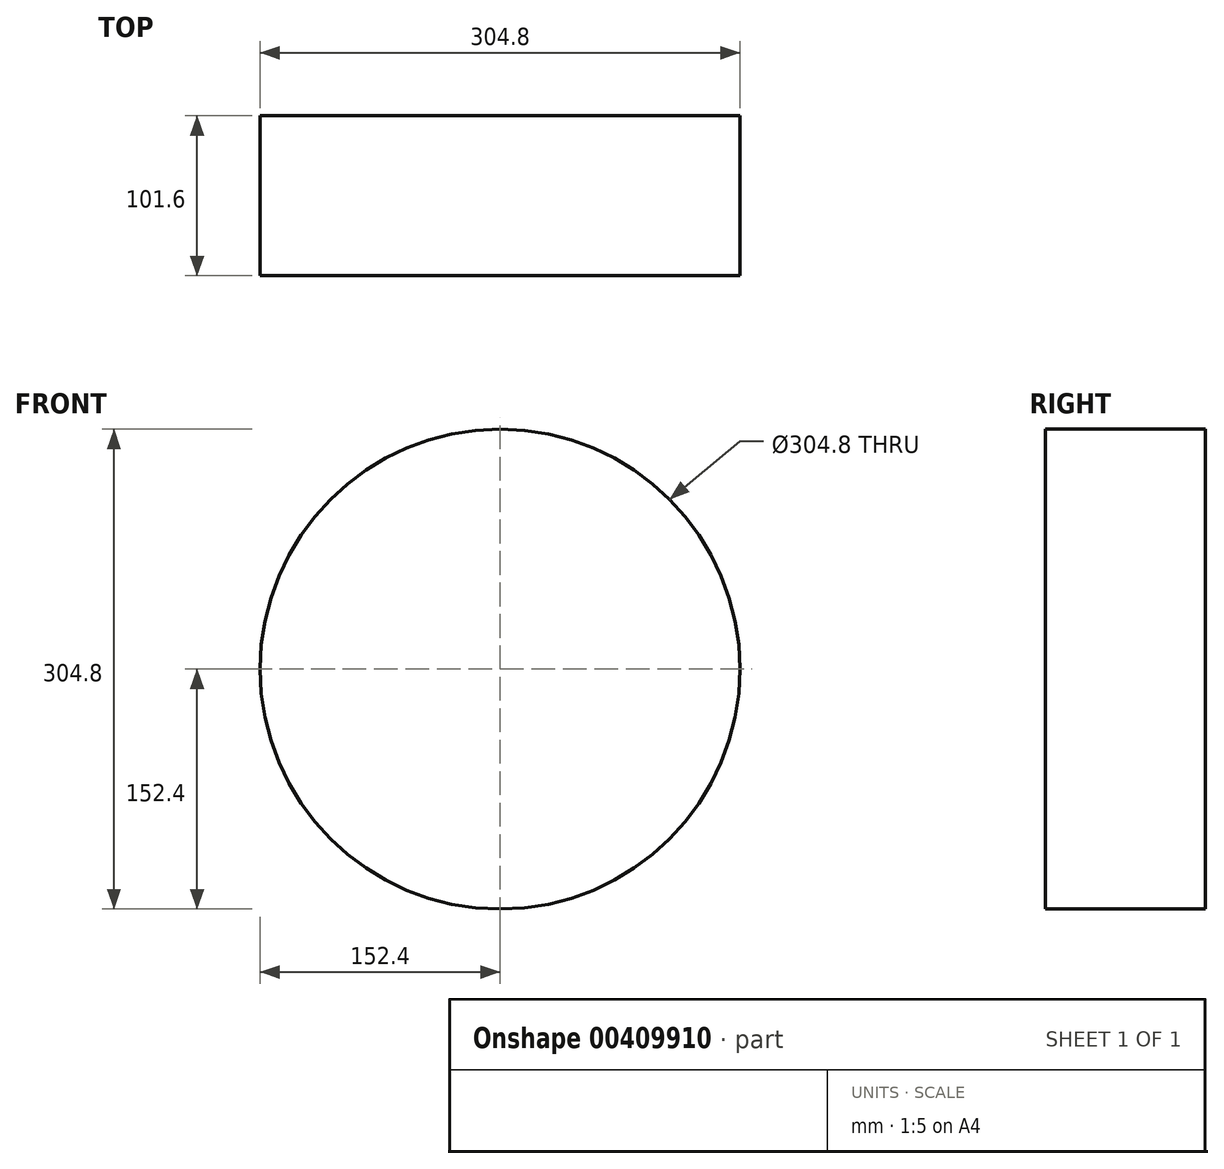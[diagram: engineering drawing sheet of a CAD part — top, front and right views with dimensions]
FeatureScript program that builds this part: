
annotation { "Feature Type Name" : "Feature", "Feature Type Description" : "" }
export const myFeature = defineFeature(function(context is Context, id is Id, definition is map)
    precondition{}
    {
        {
            var Q0;
            Q0=qCreatedBy(makeId("Front.planeOp"),FACE);
            var sketch = newSketch(context, id + "F0", { "sketchPlane" : qUnion([Q0])});
            skCircle(sketch, "E0", {"center": v(0, 0) * mm, "radius": 152.4 * mm});
            skSolve(sketch);
        }
        {
            var Q0;
            Q0=sQuery(id+"F0.wireOp",EDGE,"E0");
            extrude(context, id + "F1", {"bodyType" : ToolBodyType.SURFACE, "surfaceEntities" : qUnion([Q0]), "oppositeDirection" : true, "depth" : 101.6 * mm});
        }
    });
